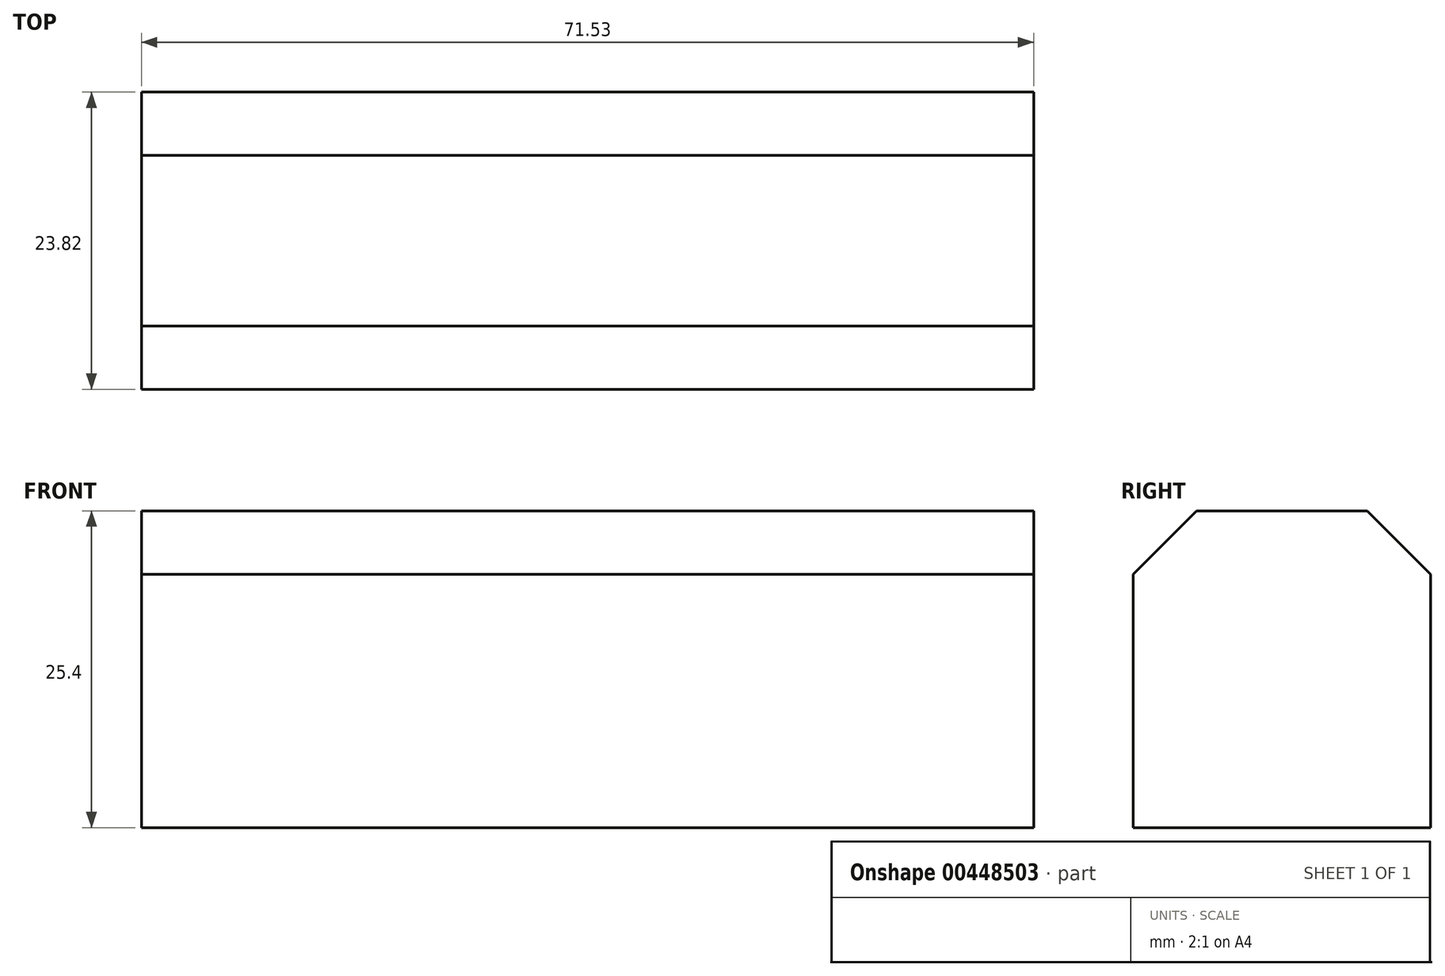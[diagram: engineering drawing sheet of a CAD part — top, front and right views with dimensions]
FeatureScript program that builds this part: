
annotation { "Feature Type Name" : "Feature", "Feature Type Description" : "" }
export const myFeature = defineFeature(function(context is Context, id is Id, definition is map)
    precondition{}
    {
        {
            var Q0;
            Q0=qCreatedBy(makeId("Top.planeOp"),FACE);
            var sketch = newSketch(context, id + "F0", { "sketchPlane" : qUnion([Q0])});
            skLineSegment(sketch, "E0.bottom", {"start": v(0, 0) * mm, "end": v(-71.53, 0) * mm});
            skLineSegment(sketch, "E0.top", {"start": v(0, -23.82) * mm, "end": v(-71.53, -23.82) * mm});
            skLineSegment(sketch, "E0.left", {"start": v(0, 0) * mm, "end": v(0, -23.82) * mm});
            skLineSegment(sketch, "E0.right", {"start": v(-71.53, 0) * mm, "end": v(-71.53, -23.82) * mm});
            skSolve(sketch);
        }
        {
            var Q0;
            Q0 = qSketchRegion(id + "F0", true);
            extrude(context, id + "F1", {"entities" : qUnion([Q0]), "depth" : 25.4 * mm});
        }
        {
            var Q0;
            Q0=makeQuery(id+"F1.opExtrude","CAP_EDGE",EDGE,{"disambiguationData":[OSD([sQuery(id+"F0.wireOp",EDGE,"E0.top")])],"isStart":false});
            var Q1;
            Q1=makeQuery(id+"F1.opExtrude","CAP_EDGE",EDGE,{"disambiguationData":[OSD([sQuery(id+"F0.wireOp",EDGE,"E0.bottom")])],"isStart":false});
            chamfer(context, id + "F2", {"entities" : qUnion([Q0, Q1]), "width" : 5.08 * mm, "tangentPropagation" : true});
        }
    });
